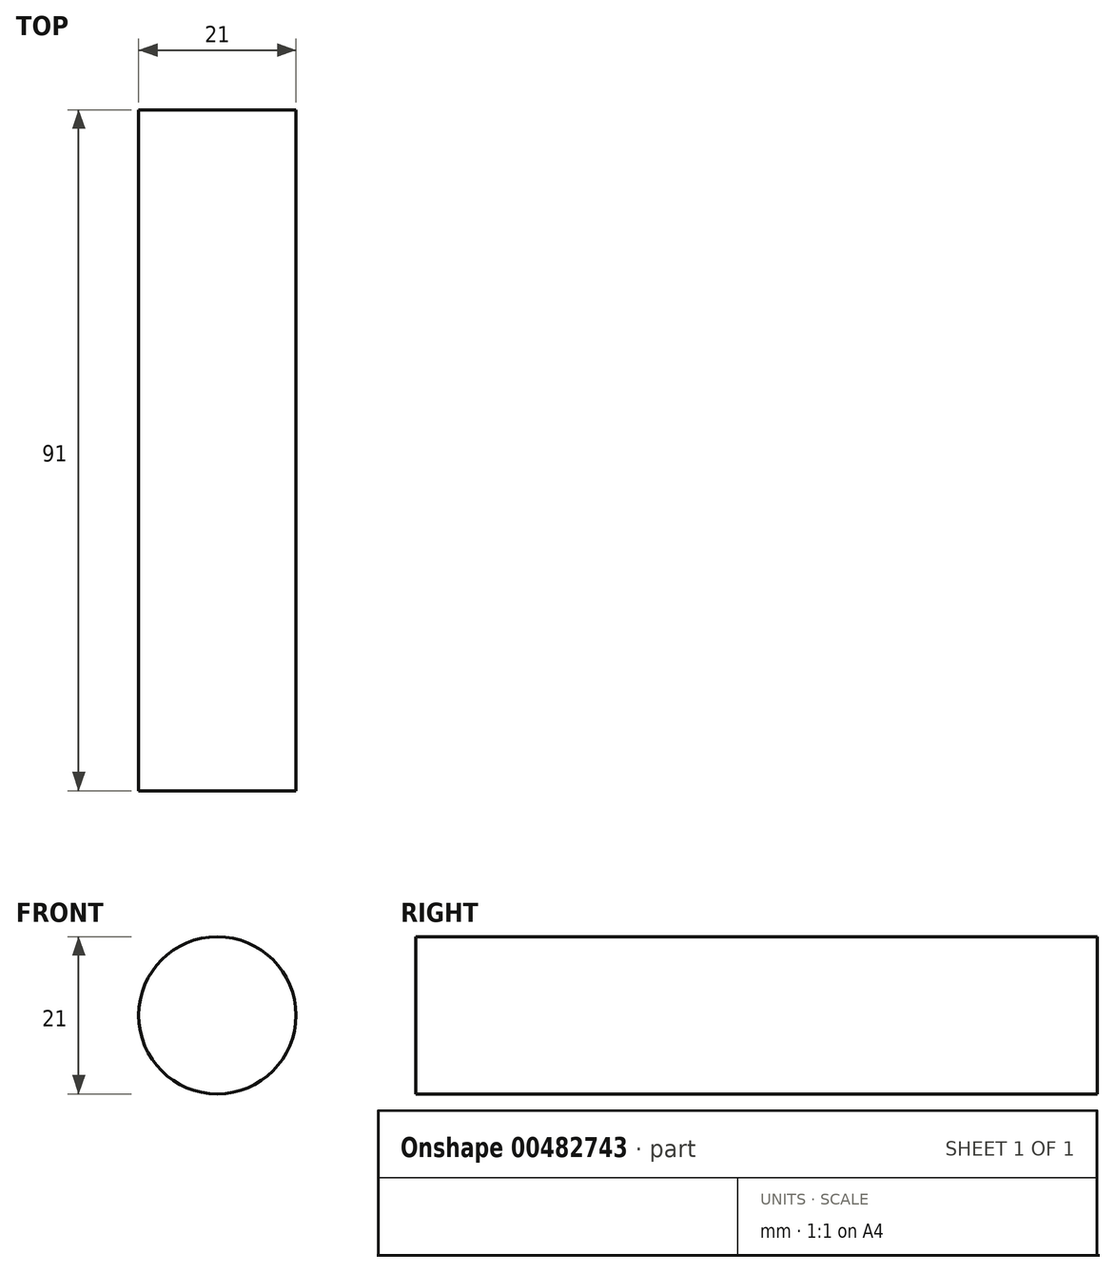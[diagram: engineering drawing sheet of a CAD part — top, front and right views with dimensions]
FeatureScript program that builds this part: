
annotation { "Feature Type Name" : "Feature", "Feature Type Description" : "" }
export const myFeature = defineFeature(function(context is Context, id is Id, definition is map)
    precondition{}
    {
        {
            var Q0;
            Q0=qCreatedBy(makeId("Front.planeOp"),FACE);
            var sketch = newSketch(context, id + "F0", { "sketchPlane" : qUnion([Q0])});
            skCircle(sketch, "E0", {"center": v(0, 0) * mm, "radius": 10.5 * mm});
            skSolve(sketch);
        }
        {
            var Q0;
            Q0=makeQuery(id+"F0.imprint","IMPRINT",FACE,{"disambiguationData":[TD([[makeQuery(id+"F0.imprint","IMPRINT",EDGE,{"derivedFrom":sQuery(id+"F0.wireOp",EDGE,"E0")}),1.0]])]});
            extrude(context, id + "F1", {"entities" : qUnion([Q0]), "depth" : 91 * mm});
        }
    });
